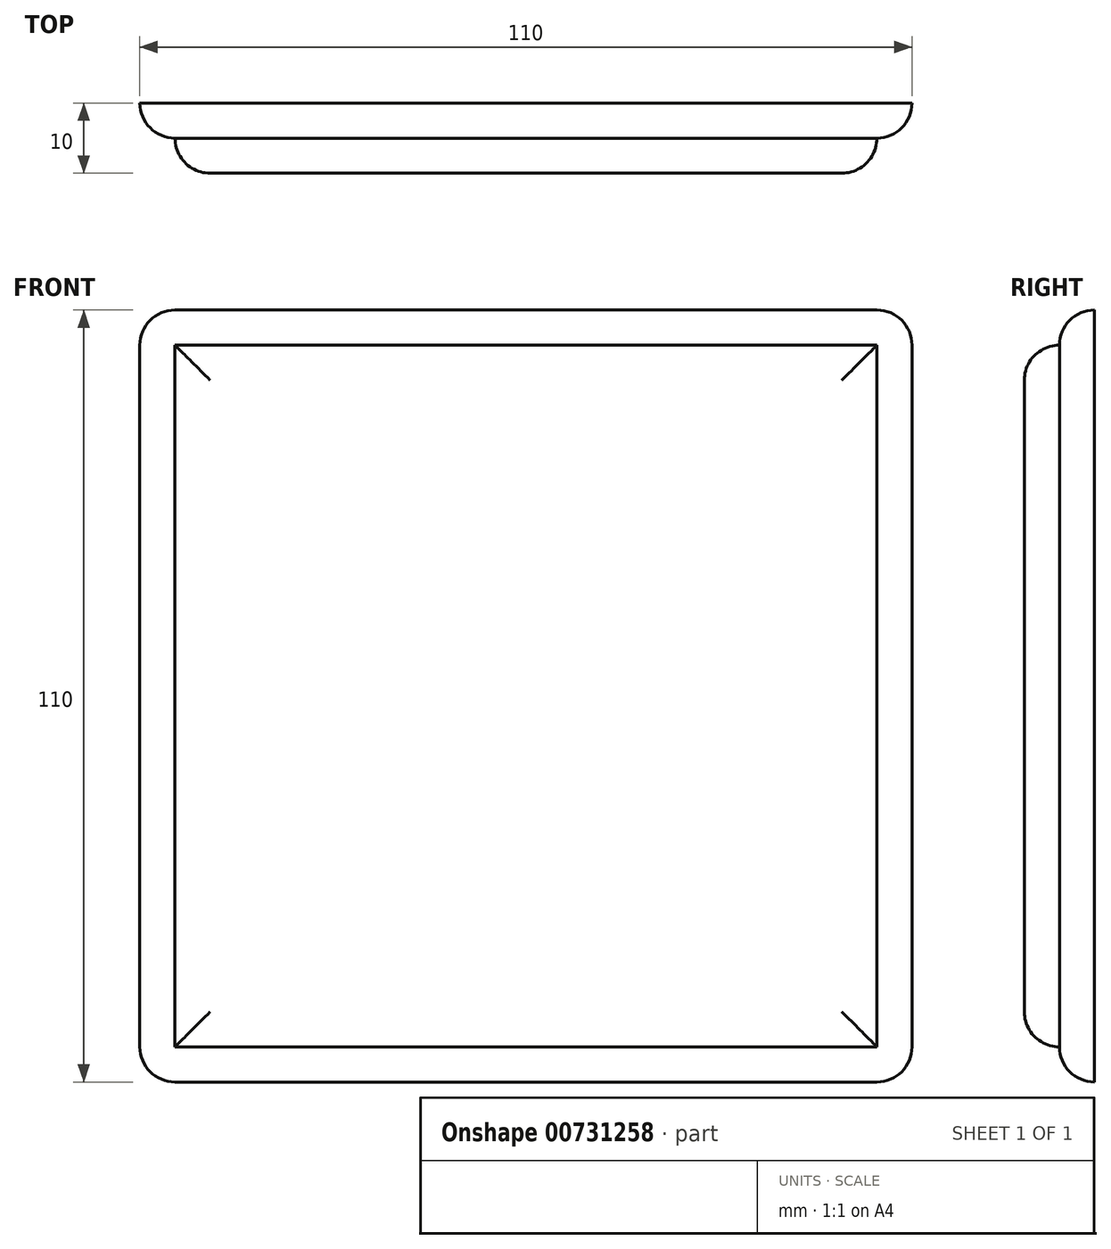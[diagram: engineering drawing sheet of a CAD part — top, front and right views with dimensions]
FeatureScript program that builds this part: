
annotation { "Feature Type Name" : "Feature", "Feature Type Description" : "" }
export const myFeature = defineFeature(function(context is Context, id is Id, definition is map)
    precondition{}
    {
        {
            var Q0;
            Q0=qCreatedBy(makeId("Front.planeOp"),FACE);
            var sketch = newSketch(context, id + "F0", { "sketchPlane" : qUnion([Q0])});
            skLineSegment(sketch, "E0.bottom", {"start": v(-50, 50) * mm, "end": v(50, 50) * mm});
            skLineSegment(sketch, "E0.top", {"start": v(-50, -50) * mm, "end": v(50, -50) * mm});
            skLineSegment(sketch, "E0.left", {"start": v(-50, 50) * mm, "end": v(-50, -50) * mm});
            skLineSegment(sketch, "E0.right", {"start": v(50, 50) * mm, "end": v(50, -50) * mm});
            skSolve(sketch);
        }
        {
            var Q0;
            Q0 = qSketchRegion(id + "F0", true);
            extrude(context, id + "F1", {"entities" : qUnion([Q0]), "depth" : 5 * mm, "offsetDistance" : 25 * mm});
        }
        {
            var Q0;
            Q0=makeQuery(id+"F1.opExtrude","CAP_FACE",FACE,{"disambiguationData":[OSD([sQuery(id+"F0.wireOp",EDGE,"E0.bottom"),sQuery(id+"F0.wireOp",EDGE,"E0.top"),sQuery(id+"F0.wireOp",EDGE,"E0.left"),sQuery(id+"F0.wireOp",EDGE,"E0.right")])],"isStart":true});
            var sketch = newSketch(context, id + "F2", { "sketchPlane" : qUnion([Q0])});
            skLineSegment(sketch, "E1.bottom", {"start": v(55, -55) * mm, "end": v(-55, -55) * mm});
            skLineSegment(sketch, "E1.top", {"start": v(55, 55) * mm, "end": v(-55, 55) * mm});
            skLineSegment(sketch, "E1.left", {"start": v(55, -55) * mm, "end": v(55, 55) * mm});
            skLineSegment(sketch, "E1.right", {"start": v(-55, -55) * mm, "end": v(-55, 55) * mm});
            skSolve(sketch);
        }
        {
            var Q0;
            Q0 = qSketchRegion(id + "F2", true);
            extrude(context, id + "F3", {"entities" : qUnion([Q0]), "operationType" : NewBodyOperationType.ADD, "depth" : 5 * mm, "offsetDistance" : 25 * mm});
        }
        {
            var Q0;
            Q0=makeQuery(id+"F3.opExtrude","SWEPT_EDGE",EDGE,{"disambiguationData":[OSD([sQuery(id+"F2.wireOp",EDGE,"E1.bottom"),sQuery(id+"F2.wireOp",EDGE,"E1.left")])]});
            var Q1;
            Q1=makeQuery(id+"F3.opExtrude","SWEPT_EDGE",EDGE,{"disambiguationData":[OSD([sQuery(id+"F2.wireOp",EDGE,"E1.bottom"),sQuery(id+"F2.wireOp",EDGE,"E1.right")])]});
            var Q2;
            Q2=makeQuery(id+"F3.opExtrude","SWEPT_EDGE",EDGE,{"disambiguationData":[OSD([sQuery(id+"F2.wireOp",EDGE,"E1.top"),sQuery(id+"F2.wireOp",EDGE,"E1.right")])]});
            var Q3;
            Q3=makeQuery(id+"F3.opExtrude","SWEPT_EDGE",EDGE,{"disambiguationData":[OSD([sQuery(id+"F2.wireOp",EDGE,"E1.top"),sQuery(id+"F2.wireOp",EDGE,"E1.left")])]});
            fillet(context, id + "F4", {"entities" : qUnion([Q0, Q1, Q2, Q3]), "radius" : 5 * mm, "tangentPropagation" : true, "allowEdgeOverflow" : false});
        }
        {
            var Q0;
            Q0=makeQuery(id+"F1.opExtrude","CAP_EDGE",EDGE,{"disambiguationData":[OSD([sQuery(id+"F0.wireOp",EDGE,"E0.bottom")])],"isStart":false});
            var Q1;
            Q1=makeQuery(id+"F1.opExtrude","CAP_EDGE",EDGE,{"disambiguationData":[OSD([sQuery(id+"F0.wireOp",EDGE,"E0.right")])],"isStart":false});
            var Q2;
            Q2=makeQuery(id+"F1.opExtrude","CAP_EDGE",EDGE,{"disambiguationData":[OSD([sQuery(id+"F0.wireOp",EDGE,"E0.top")])],"isStart":false});
            var Q3;
            Q3=makeQuery(id+"F1.opExtrude","CAP_EDGE",EDGE,{"disambiguationData":[OSD([sQuery(id+"F0.wireOp",EDGE,"E0.left")])],"isStart":false});
            fillet(context, id + "F5", {"entities" : qUnion([Q0, Q1, Q2, Q3]), "radius" : 5 * mm, "tangentPropagation" : true, "allowEdgeOverflow" : false});
        }
        {
            var Q0;
            Q0=makeQuery(id+"F3.opExtrude","CAP_EDGE",EDGE,{"disambiguationData":[OSD([sQuery(id+"F2.wireOp",EDGE,"E1.bottom")])],"isStart":true});
            fillet(context, id + "F6", {"entities" : qUnion([Q0]), "radius" : 5 * mm, "tangentPropagation" : true, "allowEdgeOverflow" : false});
        }
    });
